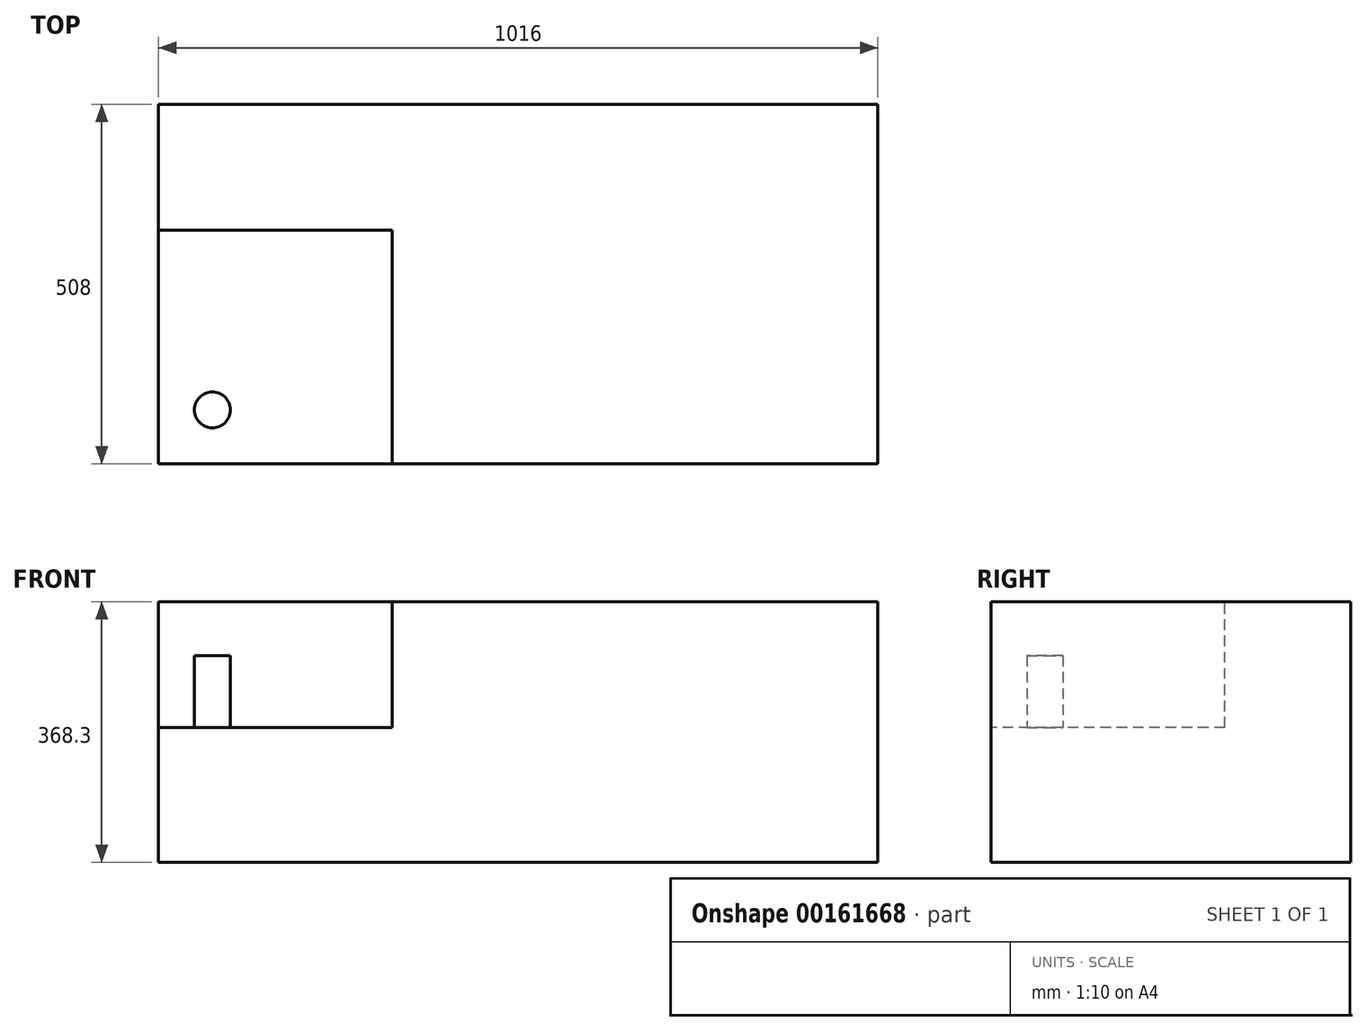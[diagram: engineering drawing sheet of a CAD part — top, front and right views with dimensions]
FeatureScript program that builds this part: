
annotation { "Feature Type Name" : "Feature", "Feature Type Description" : "" }
export const myFeature = defineFeature(function(context is Context, id is Id, definition is map)
    precondition{}
    {
        {
            var Q0;
            Q0=qCreatedBy(makeId("Top.planeOp"),FACE);
            var sketch = newSketch(context, id + "F0", { "sketchPlane" : qUnion([Q0])});
            skLineSegment(sketch, "E0.bottom", {"start": v(-508, 254) * mm, "end": v(508, 254) * mm});
            skLineSegment(sketch, "E0.top", {"start": v(-508, -254) * mm, "end": v(508, -254) * mm});
            skLineSegment(sketch, "E0.left", {"start": v(-508, 254) * mm, "end": v(-508, -254) * mm});
            skLineSegment(sketch, "E0.right", {"start": v(508, 254) * mm, "end": v(508, -254) * mm});
            skPoint(sketch, "E0.middle", {"position": v(0, 0) * mm});
            skSolve(sketch);
        }
        {
            var Q0;
            Q0 = qSketchRegion(id + "F0", true);
            extrude(context, id + "F1", {"entities" : qUnion([Q0]), "depth" : 368.3 * mm});
        }
        {
            var Q0;
            Q0=makeQuery(id+"F1.opExtrude","CAP_FACE",FACE,{"disambiguationData":[OSD([sQuery(id+"F0.wireOp",EDGE,"E0.bottom"),sQuery(id+"F0.wireOp",EDGE,"E0.top"),sQuery(id+"F0.wireOp",EDGE,"E0.left"),sQuery(id+"F0.wireOp",EDGE,"E0.right")])],"isStart":false});
            var sketch = newSketch(context, id + "F2", { "sketchPlane" : qUnion([Q0])});
            skLineSegment(sketch, "E1.bottom", {"start": v(-508, -254) * mm, "end": v(-177.8, -254) * mm});
            skLineSegment(sketch, "E1.top", {"start": v(-508, 76.2) * mm, "end": v(-177.8, 76.2) * mm});
            skLineSegment(sketch, "E1.left", {"start": v(-508, -254) * mm, "end": v(-508, 76.2) * mm});
            skLineSegment(sketch, "E1.right", {"start": v(-177.8, -254) * mm, "end": v(-177.8, 76.2) * mm});
            skSolve(sketch);
        }
        {
            var Q0;
            Q0 = qSketchRegion(id + "F2", true);
            extrude(context, id + "F3", {"entities" : qUnion([Q0]), "operationType" : NewBodyOperationType.REMOVE, "oppositeDirection" : true, "depth" : 177.8 * mm});
        }
        {
            var Q0;
            Q0=makeQuery(id+"F3.boolean.opBoolean","COPY",FACE,{"derivedFrom":makeQuery(id+"F3.opExtrude","CAP_FACE",FACE,{"disambiguationData":[OSD([sQuery(id+"F2.wireOp",EDGE,"E1.bottom"),sQuery(id+"F2.wireOp",EDGE,"E1.top"),sQuery(id+"F2.wireOp",EDGE,"E1.left"),sQuery(id+"F2.wireOp",EDGE,"E1.right")])],"isStart":false})});
            var sketch = newSketch(context, id + "F4", { "sketchPlane" : qUnion([Q0])});
            skCircle(sketch, "E2", {"center": v(-431.8, -177.8) * mm, "radius": 25.4 * mm});
            skSolve(sketch);
        }
        {
            var Q0;
            Q0 = qSketchRegion(id + "F4", true);
            extrude(context, id + "F5", {"entities" : qUnion([Q0]), "operationType" : NewBodyOperationType.ADD, "depth" : 101.6 * mm});
        }
    });
